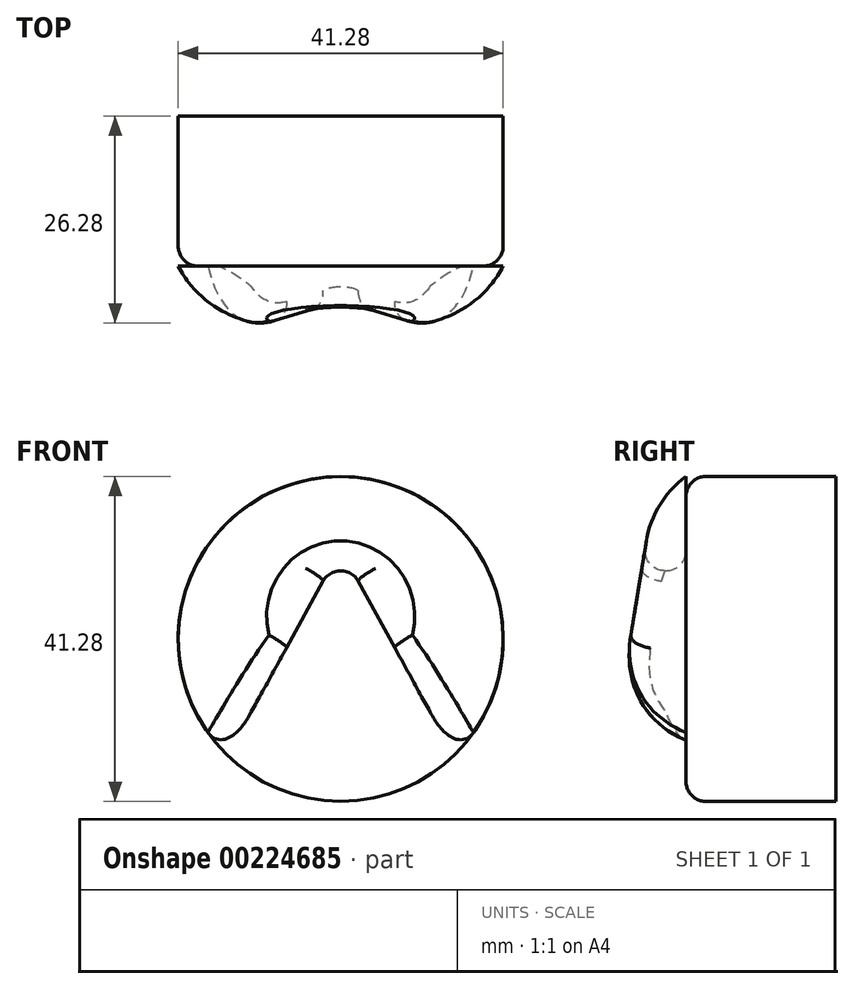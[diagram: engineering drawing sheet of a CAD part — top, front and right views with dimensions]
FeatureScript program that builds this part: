
annotation { "Feature Type Name" : "Feature", "Feature Type Description" : "" }
export const myFeature = defineFeature(function(context is Context, id is Id, definition is map)
    precondition{}
    {
        {
            var Q0;
            Q0=qCreatedBy(makeId("Front.planeOp"),FACE);
            var sketch = newSketch(context, id + "F0", { "sketchPlane" : qUnion([Q0])});
            skCircle(sketch, "E0", {"center": v(0, 0) * mm, "radius": 20.64 * mm});
            skSolve(sketch);
        }
        {
            var Q0;
            Q0 = qSketchRegion(id + "F0", true);
            extrude(context, id + "F5", {"entities" : qUnion([Q0]), "endBound" : BoundingType.SYMMETRIC, "depth" : 19.05 * mm});
        }
        {
            var Q0;
            Q0=makeQuery(id+"F5.opExtrude","CAP_FACE",FACE,{"disambiguationData":[OSD([sQuery(id+"F0.wireOp",EDGE,"E0")])],"isStart":false});
            var sketch = newSketch(context, id + "F6", { "sketchPlane" : qUnion([Q0])});
            skCircle(sketch, "E1.0", {"center": v(0, 0) * mm, "radius": 20.64 * mm});
            skLineSegment(sketch, "E2", {"start": v(-14.38, -14.8) * mm, "end": v(0, 11.4) * mm});
            skLineSegment(sketch, "E3", {"start": v(0, 11.4) * mm, "end": v(14.38, -14.8) * mm});
            skSolve(sketch);
        }
        {
            var Q0;
            {var subQ0=sQuery(id+"F6.wireOp",EDGE,"E2");Q0=makeQuery(id+"F6.imprint","IMPRINT",FACE,{"disambiguationData":[TD([[makeQuery(id+"F6.imprint","IMPRINT",EDGE,{"derivedFrom":subQ0}),1.0]])]});}
            extrude(context, id + "F1", {"entities" : qUnion([Q0]), "depth" : 9.52 * mm});
        }
        {
            var Q0;
            Q0=qCreatedBy(makeId("Right.planeOp"),FACE);
            var sketch = newSketch(context, id + "F2", { "sketchPlane" : qUnion([Q0])});
            skLineSegment(sketch, "E4", {"start": v(-19.05, 20.64) * mm, "end": v(-9.53, 20.64) * mm});
            skLineSegment(sketch, "E5.0", {"start": v(-19.05, -14.8) * mm, "end": v(-19.05, 20.64) * mm});
            skLineSegment(sketch, "E6", {"start": v(-19.05, -14.8) * mm, "end": v(-13.2, 20.75) * mm});
            skSolve(sketch);
        }
        {
            var Q0;
            Q0 = qSketchRegion(id + "F2", true);
            extrude(context, id + "F7", {"entities" : qUnion([Q0]), "operationType" : NewBodyOperationType.REMOVE, "endBound" : BoundingType.SYMMETRIC, "oppositeDirection" : true, "depth" : 2540 * mm});
        }
        {
            var Q0;
            Q0=makeQuery(id+"F7.boolean.opBoolean","INTERSECT",EDGE,{"derivedFrom":[makeQuery(id+"F1.opExtrude","SWEPT_FACE",FACE,{"disambiguationData":[OSD([sQuery(id+"F6.wireOp",EDGE,"E1.0")])]}),makeQuery(id+"F7.opExtrude","SWEPT_FACE",FACE,{"disambiguationData":[OSD([sQuery(id+"F2.wireOp",EDGE,"E6")])]})]});
            fillet(context, id + "F3", {"entities" : qUnion([Q0]), "radius" : 12.63 * mm, "tangentPropagation" : true, "allowEdgeOverflow" : false});
        }
        {
            var Q0;
            Q0=makeQuery(id+"F5.opExtrude","CAP_FACE",FACE,{"disambiguationData":[OSD([sQuery(id+"F0.wireOp",EDGE,"E0")])],"isStart":false});
            var Q1;
            Q1=makeQuery(id+"F7.boolean.opBoolean","INTERSECT",EDGE,{"derivedFrom":[makeQuery(id+"F1.opExtrude","SWEPT_FACE",FACE,{"disambiguationData":[OSD([sQuery(id+"F6.wireOp",EDGE,"E2")])]}),makeQuery(id+"F7.opExtrude","SWEPT_FACE",FACE,{"disambiguationData":[OSD([sQuery(id+"F2.wireOp",EDGE,"E6")])]})]});
            var Q2;
            Q2=makeQuery(id+"F3.opFillet","BLEND_EDGE",EDGE,{"disambiguationData":[OD(1.0)],"blendedFrom":[makeQuery(id+"F7.boolean.opBoolean","INTERSECT",EDGE,{"derivedFrom":[makeQuery(id+"F1.opExtrude","SWEPT_FACE",FACE,{"disambiguationData":[OSD([sQuery(id+"F6.wireOp",EDGE,"E1.0")])]}),makeQuery(id+"F7.opExtrude","SWEPT_FACE",FACE,{"disambiguationData":[OSD([sQuery(id+"F2.wireOp",EDGE,"E6")])]})]}),makeQuery(id+"F1.opExtrude","SWEPT_FACE",FACE,{"disambiguationData":[OSD([sQuery(id+"F6.wireOp",EDGE,"E2")])]})],"blendedInto":[makeQuery(id+"F1.opExtrude","SWEPT_FACE",FACE,{"disambiguationData":[OSD([sQuery(id+"F6.wireOp",EDGE,"E2")])]})]});
            var Q3;
            Q3=makeQuery(id+"F7.boolean.opBoolean","INTERSECT",EDGE,{"derivedFrom":[makeQuery(id+"F1.opExtrude","SWEPT_FACE",FACE,{"disambiguationData":[OSD([sQuery(id+"F6.wireOp",EDGE,"E3")])]}),makeQuery(id+"F7.opExtrude","SWEPT_FACE",FACE,{"disambiguationData":[OSD([sQuery(id+"F2.wireOp",EDGE,"E6")])]})]});
            var Q4;
            Q4=makeQuery(id+"F3.opFillet","BLEND_EDGE",EDGE,{"disambiguationData":[OD(1.0)],"blendedFrom":[makeQuery(id+"F7.boolean.opBoolean","INTERSECT",EDGE,{"derivedFrom":[makeQuery(id+"F1.opExtrude","SWEPT_FACE",FACE,{"disambiguationData":[OSD([sQuery(id+"F6.wireOp",EDGE,"E1.0")])]}),makeQuery(id+"F7.opExtrude","SWEPT_FACE",FACE,{"disambiguationData":[OSD([sQuery(id+"F2.wireOp",EDGE,"E6")])]})]}),makeQuery(id+"F1.opExtrude","SWEPT_FACE",FACE,{"disambiguationData":[OSD([sQuery(id+"F6.wireOp",EDGE,"E3")])]})],"blendedInto":[makeQuery(id+"F1.opExtrude","SWEPT_FACE",FACE,{"disambiguationData":[OSD([sQuery(id+"F6.wireOp",EDGE,"E3")])]})]});
            var Q5;
            Q5=makeQuery(id+"F3.opFillet","BLEND_EDGE",EDGE,{"disambiguationData":[OD(0.0)],"blendedFrom":[makeQuery(id+"F7.boolean.opBoolean","INTERSECT",EDGE,{"derivedFrom":[makeQuery(id+"F1.opExtrude","SWEPT_FACE",FACE,{"disambiguationData":[OSD([sQuery(id+"F6.wireOp",EDGE,"E1.0")])]}),makeQuery(id+"F7.opExtrude","SWEPT_FACE",FACE,{"disambiguationData":[OSD([sQuery(id+"F2.wireOp",EDGE,"E6")])]})]}),makeQuery(id+"F1.opExtrude","SWEPT_FACE",FACE,{"disambiguationData":[OSD([sQuery(id+"F6.wireOp",EDGE,"E3")])]})],"blendedInto":[makeQuery(id+"F1.opExtrude","SWEPT_FACE",FACE,{"disambiguationData":[OSD([sQuery(id+"F6.wireOp",EDGE,"E3")])]})]});
            var Q6;
            Q6=makeQuery(id+"F3.opFillet","BLEND_EDGE",EDGE,{"disambiguationData":[OD(0.0)],"blendedFrom":[makeQuery(id+"F7.boolean.opBoolean","INTERSECT",EDGE,{"derivedFrom":[makeQuery(id+"F1.opExtrude","SWEPT_FACE",FACE,{"disambiguationData":[OSD([sQuery(id+"F6.wireOp",EDGE,"E1.0")])]}),makeQuery(id+"F7.opExtrude","SWEPT_FACE",FACE,{"disambiguationData":[OSD([sQuery(id+"F2.wireOp",EDGE,"E6")])]})]}),makeQuery(id+"F1.opExtrude","SWEPT_FACE",FACE,{"disambiguationData":[OSD([sQuery(id+"F6.wireOp",EDGE,"E2")])]})],"blendedInto":[makeQuery(id+"F1.opExtrude","SWEPT_FACE",FACE,{"disambiguationData":[OSD([sQuery(id+"F6.wireOp",EDGE,"E2")])]})]});
            var Q7;
            Q7=makeQuery(id+"F1.opExtrude","SWEPT_FACE",FACE,{"disambiguationData":[OSD([sQuery(id+"F6.wireOp",EDGE,"E2")])]});
            var Q8;
            Q8=makeQuery(id+"F3.opFillet","BLEND_EDGE",EDGE,{"blendedFrom":[makeQuery(id+"F7.boolean.opBoolean","INTERSECT",EDGE,{"derivedFrom":[makeQuery(id+"F1.opExtrude","SWEPT_FACE",FACE,{"disambiguationData":[OSD([sQuery(id+"F6.wireOp",EDGE,"E1.0")])]}),makeQuery(id+"F7.opExtrude","SWEPT_FACE",FACE,{"disambiguationData":[OSD([sQuery(id+"F2.wireOp",EDGE,"E6")])]})]}),makeQuery(id+"F5.opExtrude","CAP_FACE",FACE,{"disambiguationData":[OSD([sQuery(id+"F0.wireOp",EDGE,"E0")])],"isStart":false})],"blendedInto":[makeQuery(id+"F5.opExtrude","CAP_FACE",FACE,{"disambiguationData":[OSD([sQuery(id+"F0.wireOp",EDGE,"E0")])],"isStart":false})]});
            var Q9;
            Q9=makeQuery(id+"F1.opExtrude","CAP_EDGE",EDGE,{"disambiguationData":[OSD([sQuery(id+"F6.wireOp",EDGE,"E2")])],"isStart":true});
            var Q10;
            Q10=makeQuery(id+"F1.opExtrude","CAP_EDGE",EDGE,{"disambiguationData":[OSD([sQuery(id+"F6.wireOp",EDGE,"E3")])],"isStart":true});
            var Q11;
            Q11=makeQuery(id+"F1.opExtrude","SWEPT_EDGE",EDGE,{"disambiguationData":[OSD([sQuery(id+"F6.wireOp",EDGE,"E2"),sQuery(id+"F6.wireOp",EDGE,"E3")])]});
            fillet(context, id + "F4", {"entities" : qUnion([Q0, Q1, Q2, Q3, Q4, Q5, Q6, Q7, Q8, Q9, Q10, Q11]), "radius" : 2.54 * mm, "tangentPropagation" : true, "allowEdgeOverflow" : false});
        }
    });
